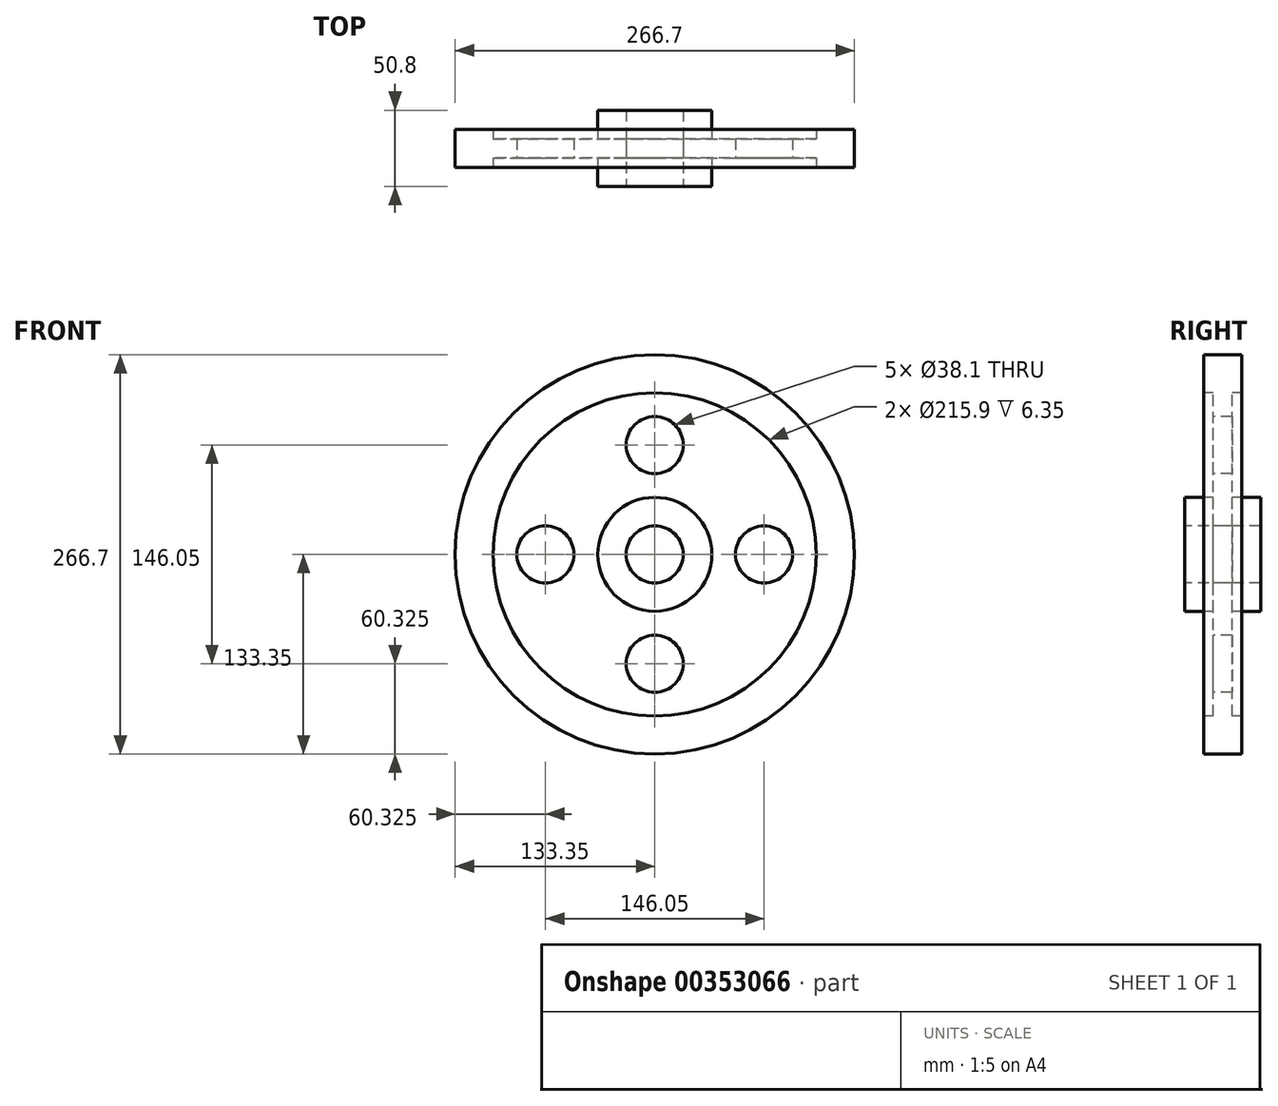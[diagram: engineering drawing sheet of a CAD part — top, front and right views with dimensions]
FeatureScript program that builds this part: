
annotation { "Feature Type Name" : "Feature", "Feature Type Description" : "" }
export const myFeature = defineFeature(function(context is Context, id is Id, definition is map)
    precondition{}
    {
        {
            var Q0;
            Q0=qCreatedBy(makeId("Right.planeOp"),FACE);
            var sketch = newSketch(context, id + "F0", { "sketchPlane" : qUnion([Q0])});
            skLineSegment(sketch, "E0", {"start": v(0, 0) * mm, "end": v(76.51, 0) * mm, "construction": true});
            skLineSegment(sketch, "E1.0", {"start": v(0, 19.05) * mm, "end": v(25.4, 19.05) * mm});
            skLineSegment(sketch, "E2.0", {"start": v(6.35, 38.1) * mm, "end": v(25.4, 38.1) * mm});
            skLineSegment(sketch, "E3.0", {"start": v(6.35, 107.95) * mm, "end": v(12.7, 107.95) * mm});
            skLineSegment(sketch, "E4", {"start": v(0, 133.35) * mm, "end": v(0, -25.4) * mm, "construction": true});
            skLineSegment(sketch, "E5.0", {"start": v(0, 133.35) * mm, "end": v(12.7, 133.35) * mm});
            skLineSegment(sketch, "E6.0", {"start": v(6.35, 107.95) * mm, "end": v(6.35, 38.1) * mm});
            skLineSegment(sketch, "E7.0", {"start": v(25.4, 38.1) * mm, "end": v(25.4, 19.05) * mm});
            skLineSegment(sketch, "E8", {"start": v(12.7, 107.95) * mm, "end": v(12.7, 133.35) * mm});
            skPoint(sketch, "E9.orphan", {"position": v(25.4, 133.35) * mm});
            skLineSegment(sketch, "E10.MirrorCS", {"start": v(-12.7, 107.95) * mm, "end": v(-12.7, 133.35) * mm});
            skLineSegment(sketch, "E11.MirrorCS", {"start": v(-6.35, 107.95) * mm, "end": v(-6.35, 38.1) * mm});
            skLineSegment(sketch, "E12.MirrorCS", {"start": v(0, 133.35) * mm, "end": v(-12.7, 133.35) * mm});
            skLineSegment(sketch, "E13.MirrorCS", {"start": v(-6.35, 107.95) * mm, "end": v(-12.7, 107.95) * mm});
            skLineSegment(sketch, "E14.MirrorCS", {"start": v(-6.35, 38.1) * mm, "end": v(-25.4, 38.1) * mm});
            skLineSegment(sketch, "E15.MirrorCS", {"start": v(-25.4, 38.1) * mm, "end": v(-25.4, 19.05) * mm});
            skLineSegment(sketch, "E16.MirrorCS", {"start": v(0, 19.05) * mm, "end": v(-25.4, 19.05) * mm});
            skSolve(sketch);
        }
        {
            var Q0;
            Q0=makeQuery(id+"F0.imprint","IMPRINT",FACE,{"disambiguationData":[TD([[makeQuery(id+"F0.imprint","IMPRINT",EDGE,{"derivedFrom":sQuery(id+"F0.wireOp",EDGE,"E1.0")}),1.0]])]});
            var Q1;
            Q1=sQuery(id+"F0.wireOp",EDGE,"E0");
            revolve(context, id + "F1", {"entities" : qUnion([Q0]), "axis" : qUnion([Q1]), "revolveType" : RevolveType.FULL});
        }
        {
            var Q0;
            Q0=makeQuery(id+"F1.opRevolve","SWEPT_FACE",FACE,{"disambiguationData":[OSD([sQuery(id+"F0.wireOp",EDGE,"E11.MirrorCS")])]});
            var sketch = newSketch(context, id + "F2", { "sketchPlane" : qUnion([Q0])});
            skLineSegment(sketch, "E17", {"start": v(0, 0) * mm, "end": v(0, 73.03) * mm});
            skCircle(sketch, "E18", {"center": v(0, 73.03) * mm, "radius": 19.05 * mm});
            skCircle(sketch, "E19.1.0", {"center": v(-73.03, 0) * mm, "radius": 19.05 * mm});
            skCircle(sketch, "E19.2.0", {"center": v(0, -73.03) * mm, "radius": 19.05 * mm});
            skCircle(sketch, "E19.3.0", {"center": v(73.03, 0) * mm, "radius": 19.05 * mm});
            skPoint(sketch, "E19.center", {"position": v(0, 0) * mm});
            skSolve(sketch);
        }
        {
            var Q0;
            Q0=makeQuery(id+"F2.imprint","IMPRINT",FACE,{"disambiguationData":[TD([[makeQuery(id+"F2.imprint","IMPRINT",EDGE,{"derivedFrom":sQuery(id+"F2.wireOp",EDGE,"E18")}),1.0]])]});
            var Q1;
            Q1=makeQuery(id+"F2.imprint","IMPRINT",FACE,{"disambiguationData":[TD([[makeQuery(id+"F2.imprint","IMPRINT",EDGE,{"derivedFrom":sQuery(id+"F2.wireOp",EDGE,"E19.1.0")}),1.0]])]});
            var Q2;
            Q2=makeQuery(id+"F2.imprint","IMPRINT",FACE,{"disambiguationData":[TD([[makeQuery(id+"F2.imprint","IMPRINT",EDGE,{"derivedFrom":sQuery(id+"F2.wireOp",EDGE,"E19.3.0")}),1.0]])]});
            var Q3;
            Q3=makeQuery(id+"F2.imprint","IMPRINT",FACE,{"disambiguationData":[TD([[makeQuery(id+"F2.imprint","IMPRINT",EDGE,{"derivedFrom":sQuery(id+"F2.wireOp",EDGE,"E19.2.0")}),1.0]])]});
            extrude(context, id + "F3", {"entities" : qUnion([Q0, Q1, Q2, Q3]), "operationType" : NewBodyOperationType.REMOVE, "oppositeDirection" : true, "depth" : 25.4 * mm});
        }
    });
